# Revit family: Porta CF  Auto e Manual
name_source: partatom
category: Doors
units: mm (PartAtom-declared; Revit-internal decimal feet)

## family parameters
Cut with Voids When Loaded = Yes
Host = Face
Room Calculation Point = No
Shared = No

## types (2) — shared parameters
Altura trilho superior = 390 mm  [stored 1.27953 ft]
Define Thermal Properties by = Schematic Type
zero-valued in all types: Default Elevation

## per-type parameters (varying)
| type | Altura Vao Luz | Automatica | Dist Motor | Height | Largura Vao Luz | Manual | Thickness | Width |
| 1000 x 2200 x 150 mm | 2200 mm | Yes | 380 mm  [stored 1.24672 ft] | 2200 mm | 1000 mm  [stored 3.28084 ft] | No | 150 mm | 1000 mm  [stored 3.28084 ft] |
| 2000 x 2500 x 100 mm | 2500 mm  [stored 8.2021 ft] | No | 30 mm  [stored 0.0984252 ft] | 2500 mm  [stored 8.2021 ft] | 3500 mm  [stored 11.4829 ft] | Yes | 100 mm  [stored 0.328084 ft] | 3500 mm  [stored 11.4829 ft] |

note: [stored X ft] marks values corroborated as IEEE doubles in the binary element streams (Revit-internal decimal feet)

## geometry (parser evidence)
native form markers: Blend x2
no freeform markers — native parametric forms only
